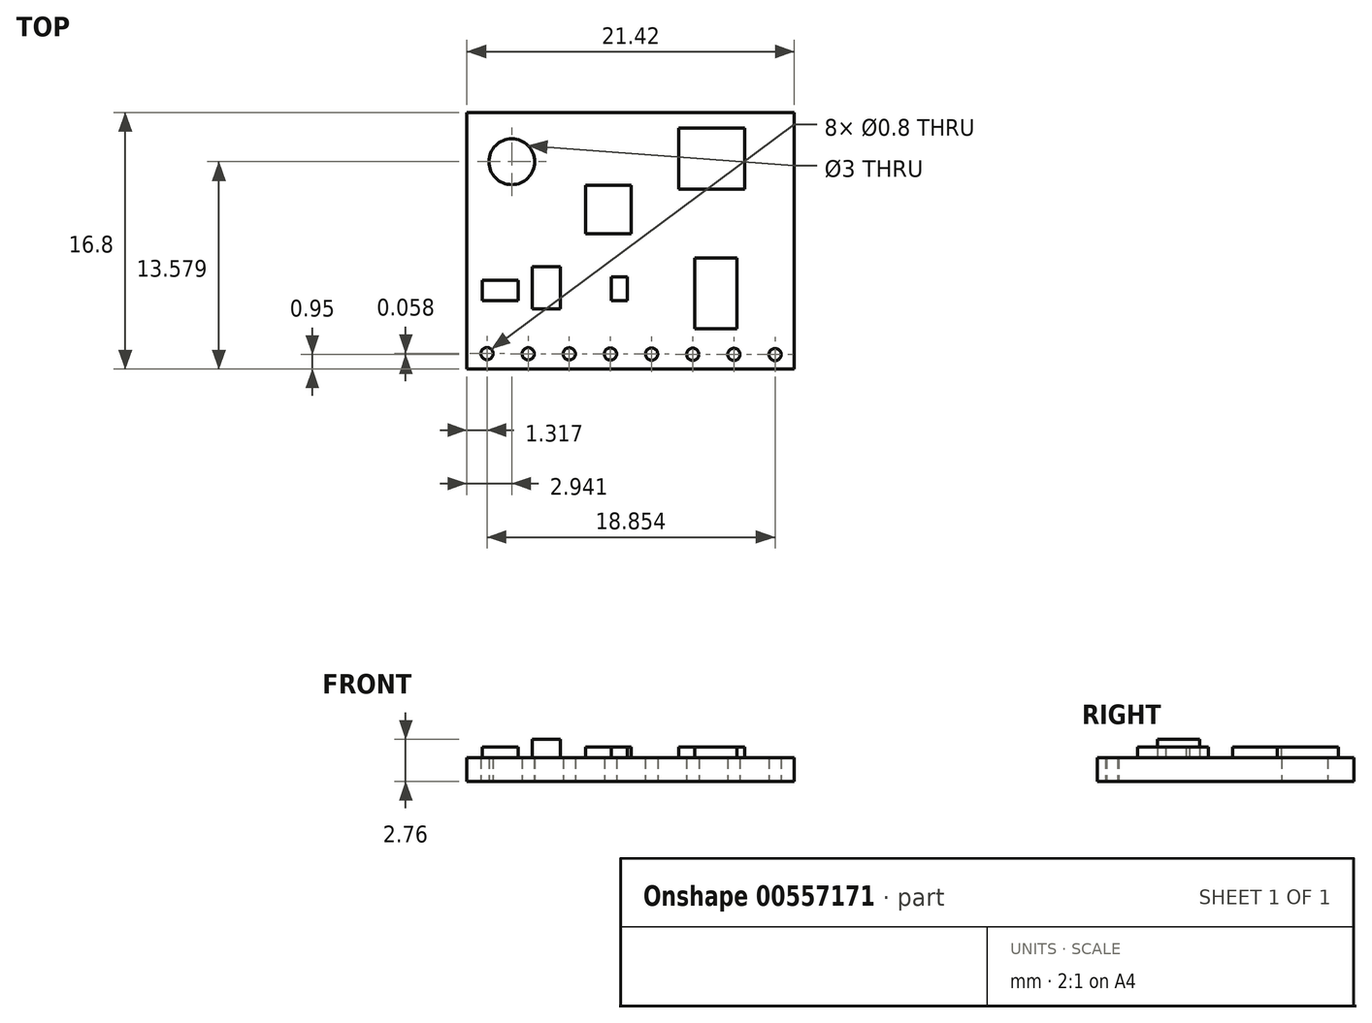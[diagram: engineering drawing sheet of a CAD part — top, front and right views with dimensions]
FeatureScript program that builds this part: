
annotation { "Feature Type Name" : "Feature", "Feature Type Description" : "" }
export const myFeature = defineFeature(function(context is Context, id is Id, definition is map)
    precondition{}
    {
        {
            var Q0;
            Q0=qCreatedBy(makeId("Top.planeOp"),FACE);
            var sketch = newSketch(context, id + "F0", { "sketchPlane" : qUnion([Q0])});
            skLineSegment(sketch, "E0.bottom", {"start": v(-10.71, 8.4) * mm, "end": v(10.72, 8.4) * mm});
            skLineSegment(sketch, "E0.top", {"start": v(-10.72, -8.4) * mm, "end": v(10.71, -8.4) * mm});
            skLineSegment(sketch, "E0.left", {"start": v(-10.71, 8.4) * mm, "end": v(-10.72, -8.4) * mm});
            skLineSegment(sketch, "E0.right", {"start": v(10.72, 8.4) * mm, "end": v(10.71, -8.4) * mm});
            skPoint(sketch, "E0.middle", {"position": v(0, 0) * mm});
            skCircle(sketch, "E1", {"center": v(-7.77, 5.18) * mm, "radius": 1.5 * mm});
            skCircle(sketch, "E2", {"center": v(-9.4, -7.4) * mm, "radius": 0.4 * mm});
            skCircle(sketch, "E3.1.0.0", {"center": v(-6.7, -7.4) * mm, "radius": 0.4 * mm});
            skCircle(sketch, "E3.2.0.0", {"center": v(-4, -7.4) * mm, "radius": 0.4 * mm});
            skCircle(sketch, "E3.3.0.0", {"center": v(-1.31, -7.42) * mm, "radius": 0.4 * mm});
            skCircle(sketch, "E3.4.0.0", {"center": v(1.38, -7.42) * mm, "radius": 0.4 * mm});
            skCircle(sketch, "E3.5.0.0", {"center": v(4.07, -7.43) * mm, "radius": 0.4 * mm});
            skCircle(sketch, "E3.6.0.0", {"center": v(6.77, -7.44) * mm, "radius": 0.4 * mm});
            skCircle(sketch, "E3.7.0.0", {"center": v(9.46, -7.45) * mm, "radius": 0.4 * mm});
            skSolve(sketch);
        }
        {
            var Q0;
            Q0=makeQuery(id+"F0.imprint","IMPRINT",FACE,{"disambiguationData":[TD([[makeQuery(id+"F0.imprint","IMPRINT",EDGE,{"derivedFrom":sQuery(id+"F0.wireOp",EDGE,"E0.bottom")}),-1.0]])]});
            extrude(context, id + "F1", {"entities" : qUnion([Q0]), "endBound" : BoundingType.SYMMETRIC, "depth" : 1.55 * mm, "offsetDistance" : 25 * mm});
        }
        {
            var Q0;
            Q0=makeQuery(id+"F1.opExtrude","CAP_FACE",FACE,{"disambiguationData":[OSD([sQuery(id+"F0.wireOp",EDGE,"E0.bottom"),sQuery(id+"F0.wireOp",EDGE,"E0.top"),sQuery(id+"F0.wireOp",EDGE,"E0.left"),sQuery(id+"F0.wireOp",EDGE,"E0.right"),sQuery(id+"F0.wireOp",EDGE,"E1"),sQuery(id+"F0.wireOp",EDGE,"E2"),sQuery(id+"F0.wireOp",EDGE,"E3.1.0.0"),sQuery(id+"F0.wireOp",EDGE,"E3.2.0.0"),sQuery(id+"F0.wireOp",EDGE,"E3.3.0.0"),sQuery(id+"F0.wireOp",EDGE,"E3.4.0.0"),sQuery(id+"F0.wireOp",EDGE,"E3.5.0.0"),sQuery(id+"F0.wireOp",EDGE,"E3.6.0.0"),sQuery(id+"F0.wireOp",EDGE,"E3.7.0.0")])],"isStart":false});
            var sketch = newSketch(context, id + "F2", { "sketchPlane" : qUnion([Q0])});
            skLineSegment(sketch, "E4.bottom", {"start": v(3.16, 3.38) * mm, "end": v(7.47, 3.38) * mm});
            skLineSegment(sketch, "E4.top", {"start": v(3.16, 7.38) * mm, "end": v(7.47, 7.38) * mm});
            skLineSegment(sketch, "E4.left", {"start": v(3.16, 3.38) * mm, "end": v(3.16, 7.38) * mm});
            skLineSegment(sketch, "E4.right", {"start": v(7.47, 3.38) * mm, "end": v(7.47, 7.38) * mm});
            skPoint(sketch, "E4.middle", {"position": v(5.32, 5.38) * mm});
            skLineSegment(sketch, "E5.bottom", {"start": v(4.2, -5.75) * mm, "end": v(6.96, -5.75) * mm});
            skLineSegment(sketch, "E5.top", {"start": v(4.2, -1.14) * mm, "end": v(6.96, -1.14) * mm});
            skLineSegment(sketch, "E5.left", {"start": v(4.2, -5.75) * mm, "end": v(4.2, -1.14) * mm});
            skLineSegment(sketch, "E5.right", {"start": v(6.96, -5.75) * mm, "end": v(6.96, -1.14) * mm});
            skPoint(sketch, "E5.middle", {"position": v(5.58, -3.45) * mm});
            skLineSegment(sketch, "E6.bottom", {"start": v(-2.94, 0.45) * mm, "end": v(0.04, 0.45) * mm});
            skLineSegment(sketch, "E6.top", {"start": v(-2.94, 3.63) * mm, "end": v(0.04, 3.63) * mm});
            skLineSegment(sketch, "E6.left", {"start": v(-2.94, 0.45) * mm, "end": v(-2.94, 3.63) * mm});
            skLineSegment(sketch, "E6.right", {"start": v(0.04, 0.45) * mm, "end": v(0.04, 3.63) * mm});
            skPoint(sketch, "E6.middle", {"position": v(-1.45, 2.04) * mm});
            skLineSegment(sketch, "E7.bottom", {"start": v(-9.71, -3.9) * mm, "end": v(-7.35, -3.9) * mm});
            skLineSegment(sketch, "E7.top", {"start": v(-9.71, -2.57) * mm, "end": v(-7.35, -2.57) * mm});
            skLineSegment(sketch, "E7.left", {"start": v(-9.71, -3.9) * mm, "end": v(-9.71, -2.57) * mm});
            skLineSegment(sketch, "E7.right", {"start": v(-7.35, -3.9) * mm, "end": v(-7.35, -2.57) * mm});
            skPoint(sketch, "E7.middle", {"position": v(-8.53, -3.24) * mm});
            skLineSegment(sketch, "E8.bottom", {"start": v(-1.25, -3.9) * mm, "end": v(-0.22, -3.9) * mm});
            skLineSegment(sketch, "E8.top", {"start": v(-1.25, -2.37) * mm, "end": v(-0.22, -2.37) * mm});
            skLineSegment(sketch, "E8.left", {"start": v(-1.25, -3.9) * mm, "end": v(-1.25, -2.37) * mm});
            skLineSegment(sketch, "E8.right", {"start": v(-0.22, -3.9) * mm, "end": v(-0.22, -2.37) * mm});
            skPoint(sketch, "E8.middle", {"position": v(-0.73, -3.14) * mm});
            skPoint(sketch, "E8.cornerSnap0", {"position": v(-8.53, -3.9) * mm});
            skLineSegment(sketch, "E9.bottom", {"start": v(-6.43, -4.47) * mm, "end": v(-4.58, -4.47) * mm});
            skLineSegment(sketch, "E9.top", {"start": v(-6.43, -1.7) * mm, "end": v(-4.58, -1.7) * mm});
            skLineSegment(sketch, "E9.left", {"start": v(-6.43, -4.47) * mm, "end": v(-6.43, -1.7) * mm});
            skLineSegment(sketch, "E9.right", {"start": v(-4.58, -4.47) * mm, "end": v(-4.58, -1.7) * mm});
            skPoint(sketch, "E9.middle", {"position": v(-5.5, -3.09) * mm});
            skSolve(sketch);
        }
        {
            var Q0;
            Q0=makeQuery(id+"F2.imprint","IMPRINT",FACE,{"disambiguationData":[TD([[makeQuery(id+"F2.imprint","IMPRINT",EDGE,{"derivedFrom":sQuery(id+"F2.wireOp",EDGE,"E7.bottom")}),1.0]])]});
            var Q1;
            Q1=makeQuery(id+"F2.imprint","IMPRINT",FACE,{"disambiguationData":[TD([[makeQuery(id+"F2.imprint","IMPRINT",EDGE,{"derivedFrom":sQuery(id+"F2.wireOp",EDGE,"E8.bottom")}),1.0]])]});
            var Q2;
            Q2=makeQuery(id+"F2.imprint","IMPRINT",FACE,{"disambiguationData":[TD([[makeQuery(id+"F2.imprint","IMPRINT",EDGE,{"derivedFrom":sQuery(id+"F2.wireOp",EDGE,"E6.bottom")}),1.0]])]});
            var Q3;
            Q3=makeQuery(id+"F2.imprint","IMPRINT",FACE,{"disambiguationData":[TD([[makeQuery(id+"F2.imprint","IMPRINT",EDGE,{"derivedFrom":sQuery(id+"F2.wireOp",EDGE,"E5.bottom")}),1.0]])]});
            var Q4;
            Q4=makeQuery(id+"F2.imprint","IMPRINT",FACE,{"disambiguationData":[TD([[makeQuery(id+"F2.imprint","IMPRINT",EDGE,{"derivedFrom":sQuery(id+"F2.wireOp",EDGE,"E4.bottom")}),1.0]])]});
            extrude(context, id + "F3", {"entities" : qUnion([Q0, Q1, Q2, Q3, Q4]), "operationType" : NewBodyOperationType.ADD, "depth" : .7 * mm, "offsetDistance" : 25 * mm});
        }
        {
            var Q0;
            Q0=makeQuery(id+"F2.imprint","IMPRINT",FACE,{"disambiguationData":[TD([[makeQuery(id+"F2.imprint","IMPRINT",EDGE,{"derivedFrom":sQuery(id+"F2.wireOp",EDGE,"E9.bottom")}),1.0]])]});
            extrude(context, id + "F4", {"entities" : qUnion([Q0]), "operationType" : NewBodyOperationType.ADD, "depth" : 1.2 * mm, "offsetDistance" : 25 * mm});
        }
    });
